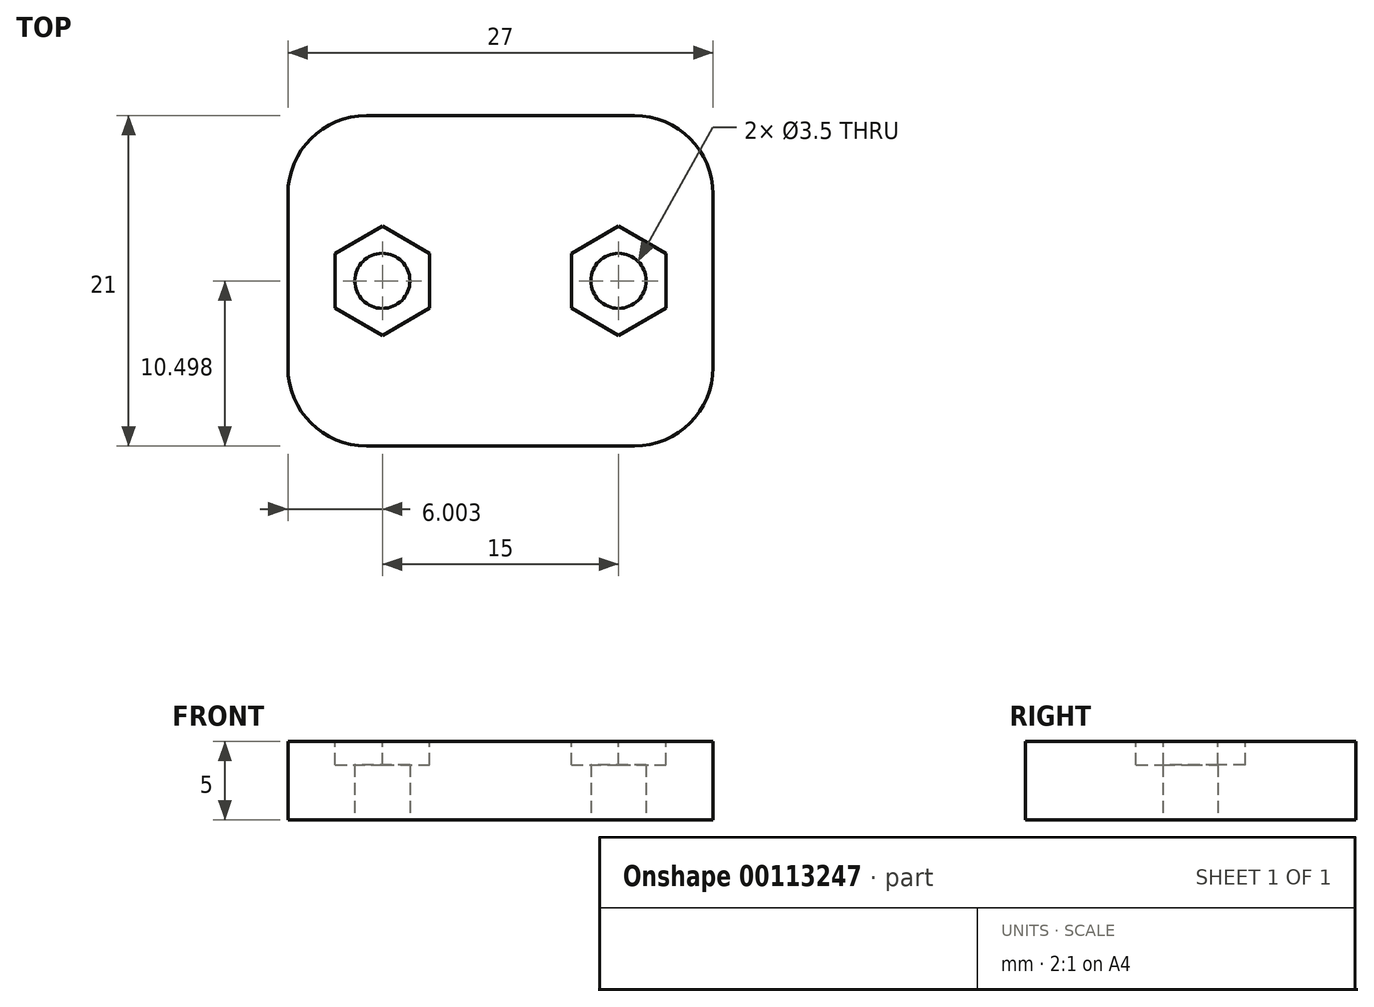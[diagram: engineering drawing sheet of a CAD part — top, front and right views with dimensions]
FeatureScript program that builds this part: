
annotation { "Feature Type Name" : "Feature", "Feature Type Description" : "" }
export const myFeature = defineFeature(function(context is Context, id is Id, definition is map)
    precondition{}
    {
        {
            var Q0;
            Q0=qCreatedBy(makeId("Top.planeOp"),FACE);
            var sketch = newSketch(context, id + "F0", { "sketchPlane" : qUnion([Q0])});
            skLineSegment(sketch, "E0.bottom", {"start": v(-4.73, 7.49) * mm, "end": v(22.27, 7.49) * mm});
            skLineSegment(sketch, "E0.top", {"start": v(-4.73, -13.51) * mm, "end": v(22.27, -13.51) * mm});
            skLineSegment(sketch, "E0.left", {"start": v(-4.73, 7.49) * mm, "end": v(-4.73, -13.51) * mm});
            skLineSegment(sketch, "E0.right", {"start": v(22.27, 7.49) * mm, "end": v(22.27, -13.51) * mm});
            skCircle(sketch, "E1", {"center": v(1.27, -3.01) * mm, "radius": 1.75 * mm});
            skCircle(sketch, "E2.1.0.0", {"center": v(16.27, -3.01) * mm, "radius": 1.75 * mm});
            skLineSegment(sketch, "E2.direction1", {"start": v(1.27, -3.01) * mm, "end": v(16.27, -3.01) * mm, "construction": true});
            skSolve(sketch);
        }
        {
            var Q0;
            Q0=makeQuery(id+"F0.imprint","IMPRINT",FACE,{"disambiguationData":[TD([[makeQuery(id+"F0.imprint","IMPRINT",EDGE,{"derivedFrom":sQuery(id+"F0.wireOp",EDGE,"E0.bottom")}),-1.0]])]});
            extrude(context, id + "F1", {"entities" : qUnion([Q0]), "depth" : 5 * mm});
        }
        {
            var Q0;
            Q0=makeQuery(id+"F1.opExtrude","SWEPT_EDGE",EDGE,{"disambiguationData":[OSD([sQuery(id+"F0.wireOp",EDGE,"E0.top"),sQuery(id+"F0.wireOp",EDGE,"E0.left")])]});
            var Q1;
            Q1=makeQuery(id+"F1.opExtrude","SWEPT_EDGE",EDGE,{"disambiguationData":[OSD([sQuery(id+"F0.wireOp",EDGE,"E0.top"),sQuery(id+"F0.wireOp",EDGE,"E0.right")])]});
            var Q2;
            Q2=makeQuery(id+"F1.opExtrude","SWEPT_EDGE",EDGE,{"disambiguationData":[OSD([sQuery(id+"F0.wireOp",EDGE,"E0.bottom"),sQuery(id+"F0.wireOp",EDGE,"E0.right")])]});
            var Q3;
            Q3=makeQuery(id+"F1.opExtrude","SWEPT_EDGE",EDGE,{"disambiguationData":[OSD([sQuery(id+"F0.wireOp",EDGE,"E0.bottom"),sQuery(id+"F0.wireOp",EDGE,"E0.left")])]});
            fillet(context, id + "F2", {"entities" : qUnion([Q0, Q1, Q2, Q3]), "radius" : 5 * mm, "tangentPropagation" : true, "allowEdgeOverflow" : false});
        }
        {
            var Q0;
            Q0=makeQuery(id+"F1.opExtrude","CAP_FACE",FACE,{"disambiguationData":[OSD([sQuery(id+"F0.wireOp",EDGE,"E0.bottom"),sQuery(id+"F0.wireOp",EDGE,"E0.top"),sQuery(id+"F0.wireOp",EDGE,"E0.left"),sQuery(id+"F0.wireOp",EDGE,"E0.right"),sQuery(id+"F0.wireOp",EDGE,"E1"),sQuery(id+"F0.wireOp",EDGE,"E2.1.0.0")])],"isStart":false});
            var sketch = newSketch(context, id + "F3", { "sketchPlane" : qUnion([Q0])});
            skCircle(sketch, "E3.cCircle", {"center": v(16.27, -3.01) * mm, "radius": 3 * mm, "construction": true});
            skLineSegment(sketch, "E3.0", {"start": v(19.27, -1.28) * mm, "end": v(19.27, -4.74) * mm});
            skLineSegment(sketch, "E3.1", {"start": v(19.27, -4.74) * mm, "end": v(16.27, -6.48) * mm});
            skLineSegment(sketch, "E3.2", {"start": v(16.27, -6.48) * mm, "end": v(13.27, -4.74) * mm});
            skLineSegment(sketch, "E3.3", {"start": v(13.27, -4.74) * mm, "end": v(13.27, -1.28) * mm});
            skLineSegment(sketch, "E3.4", {"start": v(13.27, -1.28) * mm, "end": v(16.27, 0.45) * mm});
            skLineSegment(sketch, "E3.5", {"start": v(16.27, 0.45) * mm, "end": v(19.27, -1.28) * mm});
            skPoint(sketch, "E3.0.midPoint", {"position": v(19.27, -3.01) * mm});
            skCircle(sketch, "E4.cCircle", {"center": v(1.27, -3.01) * mm, "radius": 3 * mm, "construction": true});
            skLineSegment(sketch, "E4.0", {"start": v(4.27, -1.28) * mm, "end": v(4.27, -4.74) * mm});
            skLineSegment(sketch, "E4.1", {"start": v(4.27, -4.74) * mm, "end": v(1.27, -6.48) * mm});
            skLineSegment(sketch, "E4.2", {"start": v(1.27, -6.48) * mm, "end": v(-1.73, -4.74) * mm});
            skLineSegment(sketch, "E4.3", {"start": v(-1.73, -4.74) * mm, "end": v(-1.73, -1.28) * mm});
            skLineSegment(sketch, "E4.4", {"start": v(-1.73, -1.28) * mm, "end": v(1.27, 0.45) * mm});
            skLineSegment(sketch, "E4.5", {"start": v(1.27, 0.45) * mm, "end": v(4.27, -1.28) * mm});
            skPoint(sketch, "E4.0.midPoint", {"position": v(4.27, -3.01) * mm});
            skSolve(sketch);
        }
        {
            var Q0;
            Q0=makeQuery(id+"F3.imprint","IMPRINT",FACE,{"disambiguationData":[TD([[makeQuery(id+"F3.imprint","IMPRINT",EDGE,{"derivedFrom":sQuery(id+"F3.wireOp",EDGE,"E4.0")}),-1.0]])]});
            var Q1;
            Q1=makeQuery(id+"F3.imprint","IMPRINT",FACE,{"disambiguationData":[TD([[makeQuery(id+"F3.imprint","IMPRINT",EDGE,{"derivedFrom":sQuery(id+"F3.wireOp",EDGE,"E3.0")}),-1.0]])]});
            extrude(context, id + "F4", {"entities" : qUnion([Q0, Q1]), "operationType" : NewBodyOperationType.REMOVE, "oppositeDirection" : true, "depth" : 1.5 * mm});
        }
    });
